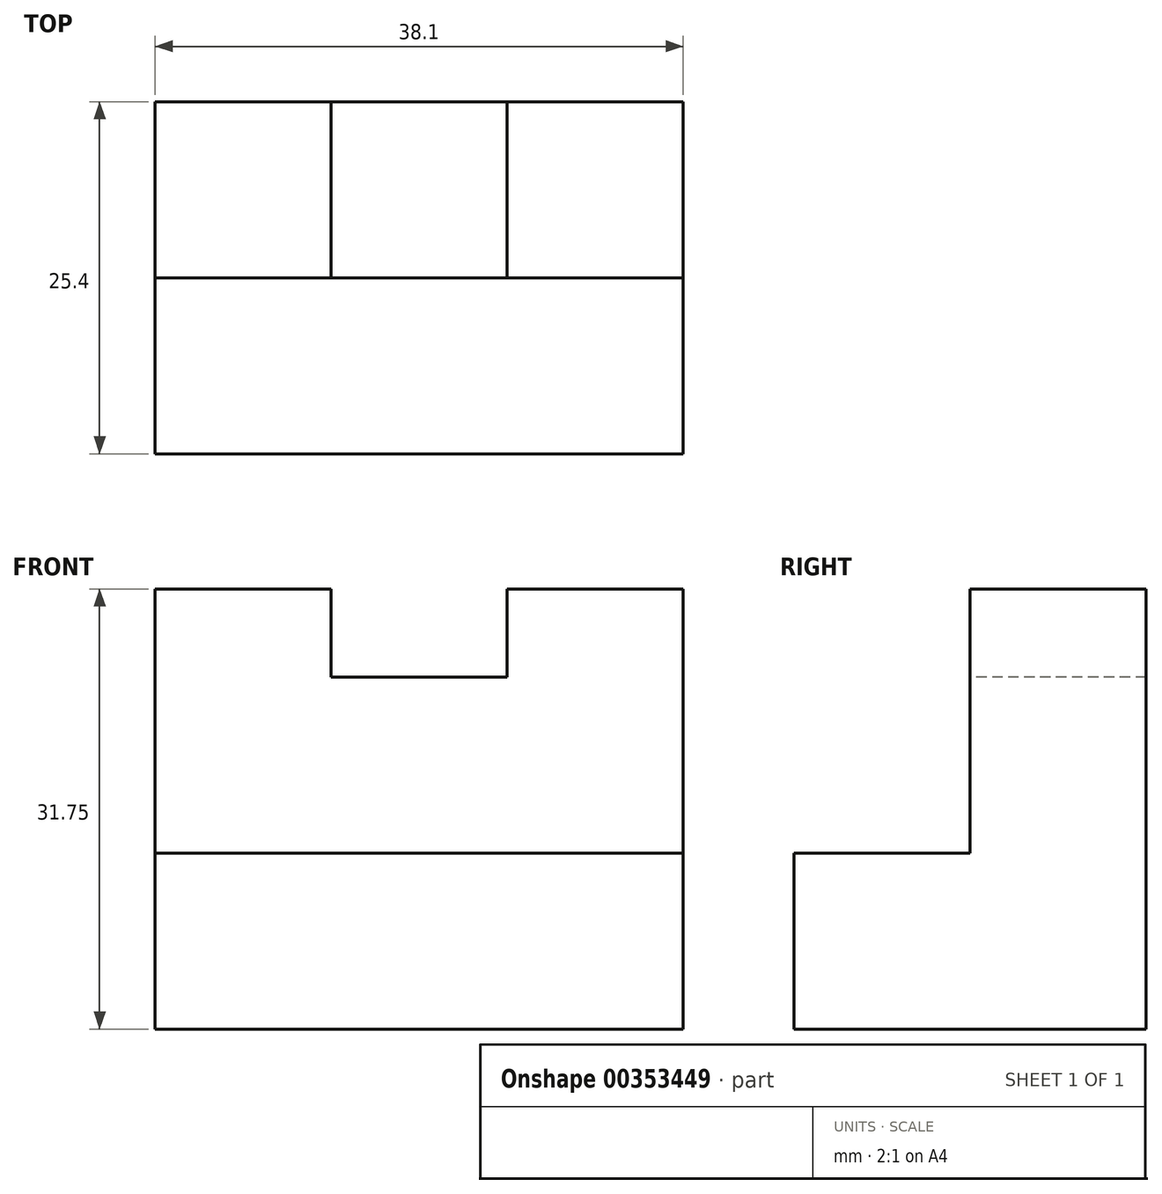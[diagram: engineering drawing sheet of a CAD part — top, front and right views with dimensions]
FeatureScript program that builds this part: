
annotation { "Feature Type Name" : "Feature", "Feature Type Description" : "" }
export const myFeature = defineFeature(function(context is Context, id is Id, definition is map)
    precondition{}
    {
        {
            var Q0;
            Q0=qCreatedBy(makeId("Right.planeOp"),FACE);
            var sketch = newSketch(context, id + "F0", { "sketchPlane" : qUnion([Q0])});
            skLineSegment(sketch, "E0", {"start": v(0, 0) * mm, "end": v(-25.4, 0) * mm});
            skLineSegment(sketch, "E1", {"start": v(-25.4, 0) * mm, "end": v(-25.4, 12.7) * mm});
            skLineSegment(sketch, "E2", {"start": v(-25.4, 12.7) * mm, "end": v(-12.7, 12.7) * mm});
            skLineSegment(sketch, "E3", {"start": v(-12.7, 12.7) * mm, "end": v(-12.7, 31.75) * mm});
            skLineSegment(sketch, "E4", {"start": v(-12.7, 31.75) * mm, "end": v(0, 31.75) * mm});
            skLineSegment(sketch, "E5", {"start": v(0, 0) * mm, "end": v(0, 31.75) * mm});
            skSolve(sketch);
        }
        {
            var Q0;
            Q0 = qSketchRegion(id + "F0", true);
            extrude(context, id + "F1", {"entities" : qUnion([Q0]), "depth" : 38.1 * mm});
        }
        {
            var Q0;
            Q0=makeQuery(id+"F1.opExtrude","SWEPT_FACE",FACE,{"disambiguationData":[OSD([sQuery(id+"F0.wireOp",EDGE,"E3")])]});
            var sketch = newSketch(context, id + "F2", { "sketchPlane" : qUnion([Q0])});
            skLineSegment(sketch, "E6", {"start": v(0, 31.75) * mm, "end": v(12.7, 31.75) * mm});
            skLineSegment(sketch, "E7", {"start": v(12.7, 31.75) * mm, "end": v(12.7, 25.4) * mm});
            skLineSegment(sketch, "E8", {"start": v(12.7, 25.4) * mm, "end": v(25.4, 25.4) * mm});
            skLineSegment(sketch, "E9", {"start": v(25.4, 25.4) * mm, "end": v(25.4, 31.75) * mm});
            skSolve(sketch);
        }
        {
            var Q0;
            {var subQ0=sQuery(id+"F2.wireOp",EDGE,"E7");Q0=makeQuery(id+"F2.imprint","IMPRINT",FACE,{"disambiguationData":[TD([[makeQuery(id+"F2.imprint","IMPRINT",EDGE,{"derivedFrom":subQ0}),1.0]])]});}
            extrude(context, id + "F3", {"entities" : qUnion([Q0]), "operationType" : NewBodyOperationType.REMOVE, "oppositeDirection" : true, "depth" : 25.4 * mm});
        }
    });
